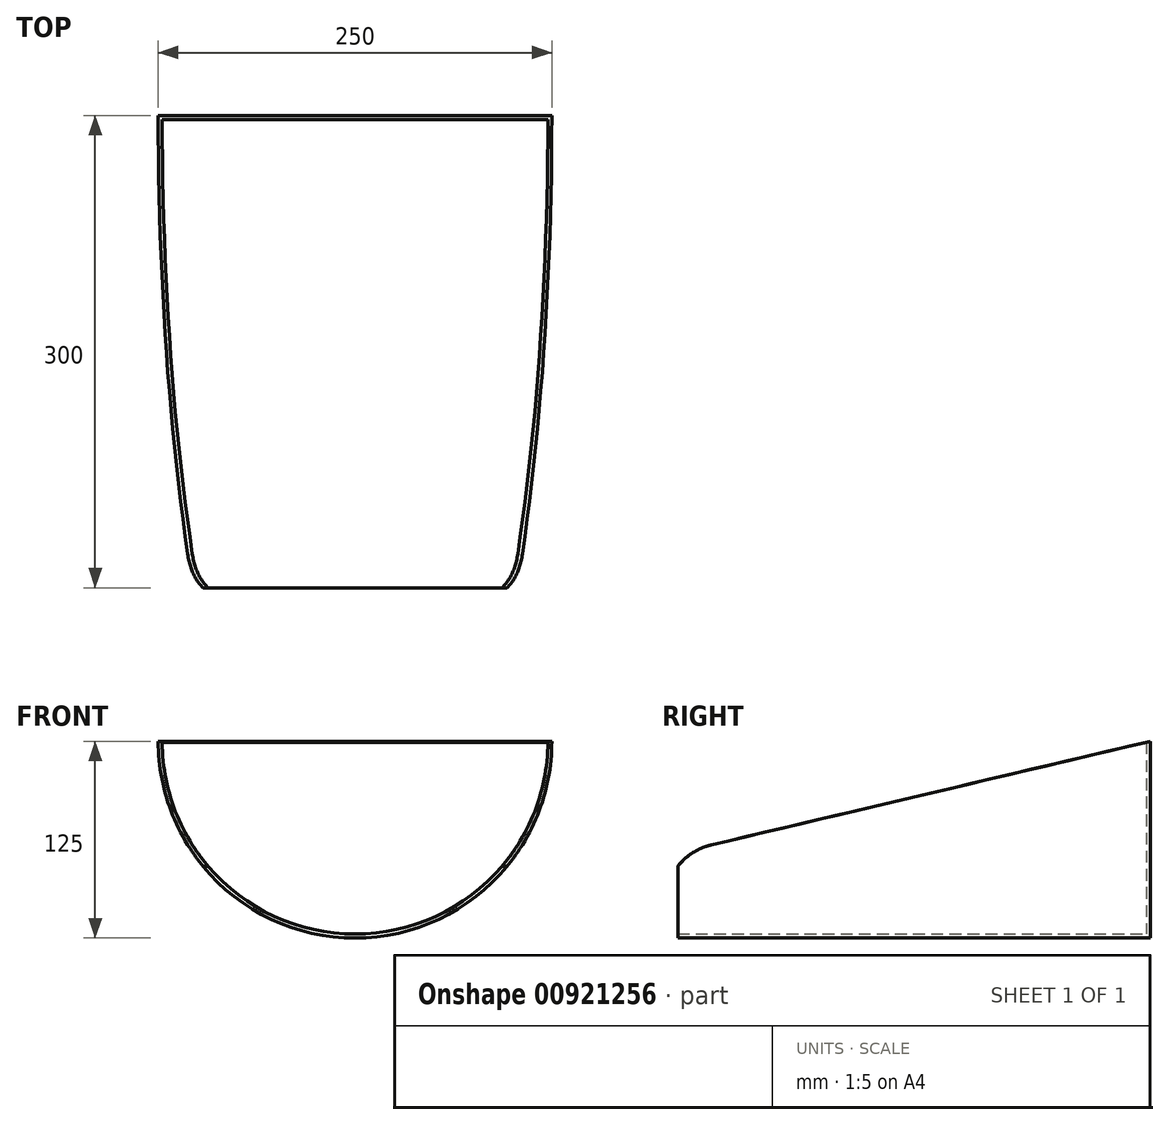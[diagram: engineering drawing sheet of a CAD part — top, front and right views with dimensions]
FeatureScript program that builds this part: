
annotation { "Feature Type Name" : "Feature", "Feature Type Description" : "" }
export const myFeature = defineFeature(function(context is Context, id is Id, definition is map)
    precondition{}
    {
        {
            var Q0;
            Q0=qCreatedBy(makeId("Front.planeOp"),FACE);
            var sketch = newSketch(context, id + "F0", { "sketchPlane" : qUnion([Q0])});
            skCircle(sketch, "E0", {"center": v(0, 0) * mm, "radius": 125 * mm});
            skSolve(sketch);
        }
        {
            var Q0;
            Q0 = qSketchRegion(id + "F0", true);
            extrude(context, id + "F1", {"entities" : qUnion([Q0]), "depth" : 300 * mm, "offsetDistance" : 25 * mm});
        }
        {
            var Q0;
            Q0=qCreatedBy(makeId("Right.planeOp"),FACE);
            cPlane(context, id + "F2", {"entities" : qUnion([Q0]), "cplaneType" : CPlaneType.OFFSET, "offset" : 125 * mm, "width" : 150 * mm, "height" : 150 * mm});
        }
        {
            var Q0;
            Q0=makeQuery(id+"F1.opExtrude","CAP_FACE",FACE,{"disambiguationData":[OSD([sQuery(id+"F0.wireOp",EDGE,"E0")])],"isStart":false});
            shell(context, id + "F3", {"entities" : qUnion([Q0]), "thickness" : 2.5 * mm});
        }
        {
            var Q0;
            Q0=qCreatedBy(id+"F2.planeOp",FACE);
            var sketch = newSketch(context, id + "F4", { "sketchPlane" : qUnion([Q0])});
            skLineSegment(sketch, "E1", {"start": v(0, 0) * mm, "end": v(-283.6, -66.96) * mm});
            skArc(sketch, "E2", {"start": v(-278.46, -65.74) * mm, "mid": v(-299.4, -78.6) * mm, "end": v(-308.55, -101.42) * mm});
            skLineSegment(sketch, "E3", {"start": v(-308.55, -101.42) * mm, "end": v(-367.8, -101.42) * mm});
            skLineSegment(sketch, "E4", {"start": v(-367.8, -101.42) * mm, "end": v(-357.28, 144.25) * mm});
            skLineSegment(sketch, "E5", {"start": v(-357.28, 144.25) * mm, "end": v(37.56, 139.17) * mm});
            skLineSegment(sketch, "E6", {"start": v(37.56, 139.17) * mm, "end": v(0, 0) * mm});
            skSolve(sketch);
        }
        {
            var Q0;
            Q0 = qSketchRegion(id + "F4", true);
            extrude(context, id + "F5", {"entities" : qUnion([Q0]), "operationType" : NewBodyOperationType.REMOVE, "oppositeDirection" : true, "depth" : 331 * mm, "offsetDistance" : 25 * mm});
        }
    });
